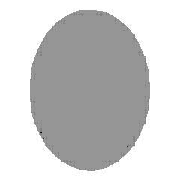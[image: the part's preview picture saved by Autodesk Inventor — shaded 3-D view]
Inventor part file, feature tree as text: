
AUTODESK INVENTOR PART (.ipt)
format: ipt  version: 2013 (Build 170138000, 138)  size: 112,128 bytes
history: native  units: mm (DEFAULTED — no unit token found)
features: other x4, plane x3, sketch x3, split x2
ambient origin geometry x8: Origin, YZ Plane, XZ Plane, XY Plane, X Axis, Y Axis, Z Axis, Center Point
bodies: Solid1 (feature_tree), Body (feature_tree)
feature tree (12):
  parser-record x1  (decoder bookkeeping rows leaked as tree rows — omitted from the tree; the rows remain in map.json)
  other  "Driven Length"
  other  "Start plane"
  other  "End plane"
  plane  "Work Plane4"
  split  "Split1"
  plane  "Work Plane5"
  split  "Split2"
  sketch  "Sketch"  dims[d2=0.0mm d4=-19.05mm d5=660.4mm d6=90.0deg d7=679.45mm]
  sketch  "Sketch2"  dims[d0=38.1mm]
  plane  "Work Plane3"
  sketch  "Sketch3"  dims[d1=679.45mm]
